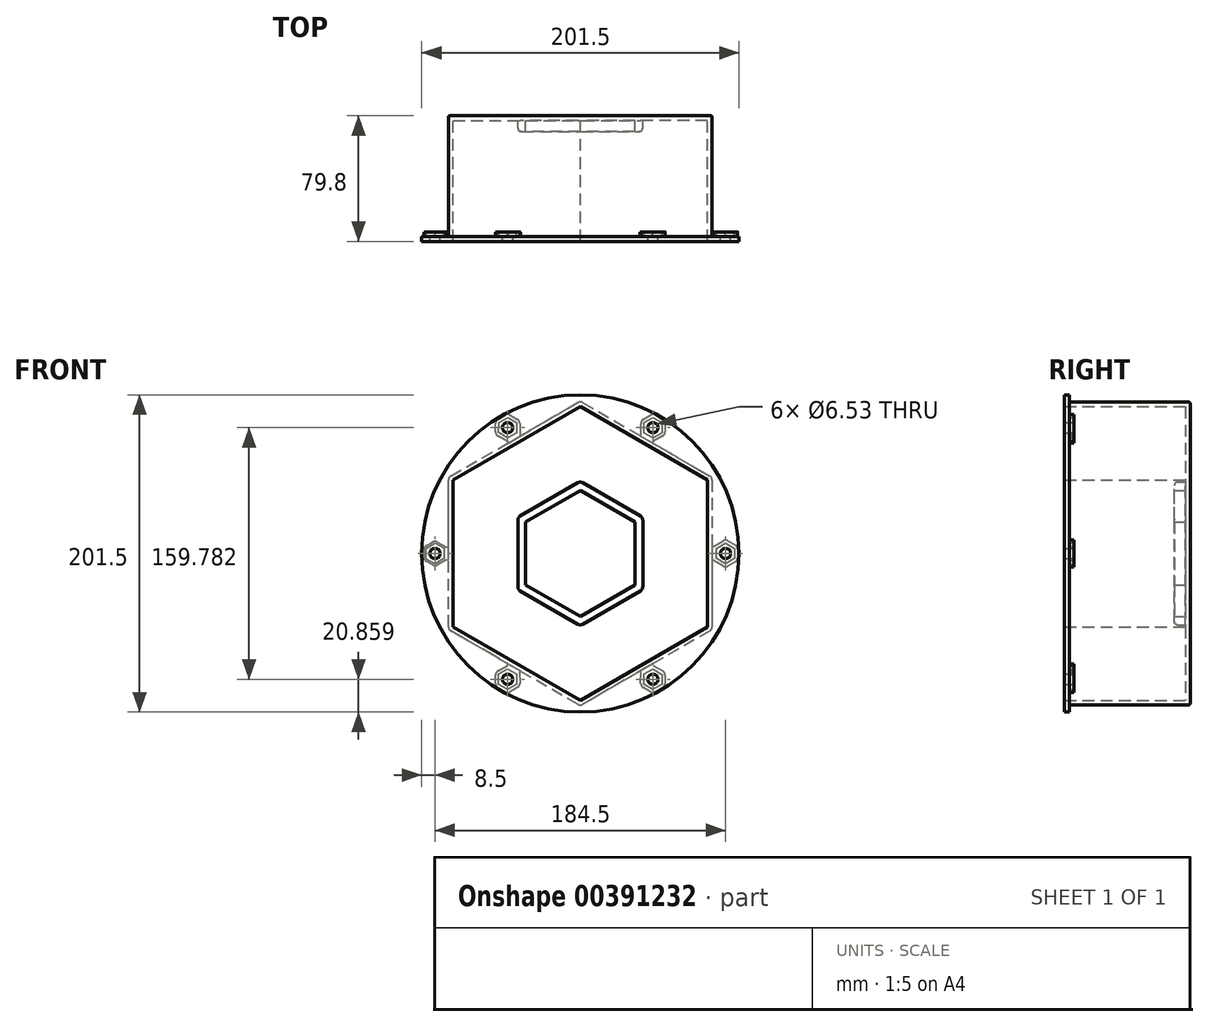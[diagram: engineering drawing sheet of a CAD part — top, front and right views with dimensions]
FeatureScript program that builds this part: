
annotation { "Feature Type Name" : "Feature", "Feature Type Description" : "" }
export const myFeature = defineFeature(function(context is Context, id is Id, definition is map)
    precondition{}
    {
        {
            var Q0;
            Q0=qCreatedBy(makeId("Front.planeOp"),FACE);
            var sketch = newSketch(context, id + "F0", { "sketchPlane" : qUnion([Q0])});
            skCircle(sketch, "E0.cCircle", {"center": v(0, 0) * mm, "radius": 80.75 * mm, "construction": true});
            skLineSegment(sketch, "E0.0", {"start": v(80.75, -46.62) * mm, "end": v(0, -93.24) * mm});
            skLineSegment(sketch, "E0.1", {"start": v(0, -93.24) * mm, "end": v(-80.75, -46.62) * mm});
            skLineSegment(sketch, "E0.2", {"start": v(-80.75, -46.62) * mm, "end": v(-80.75, 46.62) * mm});
            skLineSegment(sketch, "E0.3", {"start": v(-80.75, 46.62) * mm, "end": v(0, 93.24) * mm});
            skLineSegment(sketch, "E0.4", {"start": v(0, 93.24) * mm, "end": v(80.75, 46.62) * mm});
            skLineSegment(sketch, "E0.5", {"start": v(80.75, 46.62) * mm, "end": v(80.75, -46.62) * mm});
            skPoint(sketch, "E0.0.midPoint", {"position": v(40.38, -69.93) * mm});
            skCircle(sketch, "E1.cCircle", {"center": v(0, 0) * mm, "radius": 83.75 * mm, "construction": true});
            skLineSegment(sketch, "E1.0", {"start": v(83.75, 46.62) * mm, "end": v(83.75, -46.62) * mm});
            skLineSegment(sketch, "E1.1", {"start": v(82.25, -49.22) * mm, "end": v(1.5, -95.84) * mm});
            skLineSegment(sketch, "E1.2", {"start": v(-1.5, -95.84) * mm, "end": v(-82.25, -49.22) * mm});
            skLineSegment(sketch, "E1.3", {"start": v(-83.75, -46.62) * mm, "end": v(-83.75, 46.62) * mm});
            skLineSegment(sketch, "E1.4", {"start": v(-82.25, 49.22) * mm, "end": v(-1.5, 95.84) * mm});
            skLineSegment(sketch, "E1.5", {"start": v(1.5, 95.84) * mm, "end": v(82.25, 49.22) * mm});
            skPoint(sketch, "E1.0.midPoint", {"position": v(83.75, 0) * mm});
            skCircle(sketch, "E2", {"center": v(0, 0) * mm, "radius": 100.75 * mm});
            skCircle(sketch, "E3.cCircle", {"center": v(0, 0) * mm, "radius": 39.66 * mm, "construction": true});
            skLineSegment(sketch, "E3.0", {"start": v(38.16, -23.77) * mm, "end": v(1.5, -44.93) * mm});
            skLineSegment(sketch, "E3.1", {"start": v(-1.5, -44.93) * mm, "end": v(-38.16, -23.77) * mm});
            skLineSegment(sketch, "E3.2", {"start": v(-39.66, -21.17) * mm, "end": v(-39.66, 21.17) * mm});
            skLineSegment(sketch, "E3.3", {"start": v(-38.16, 23.77) * mm, "end": v(-1.5, 44.93) * mm});
            skLineSegment(sketch, "E3.4", {"start": v(1.5, 44.93) * mm, "end": v(38.16, 23.77) * mm});
            skLineSegment(sketch, "E3.5", {"start": v(39.66, 21.17) * mm, "end": v(39.66, -21.17) * mm});
            skPoint(sketch, "E3.0.midPoint", {"position": v(19.83, -34.35) * mm});
            skCircle(sketch, "E4.cCircle", {"center": v(0, 0) * mm, "radius": 34.66 * mm, "construction": true});
            skLineSegment(sketch, "E4.0", {"start": v(34.66, -20.01) * mm, "end": v(0, -40.03) * mm});
            skLineSegment(sketch, "E4.1", {"start": v(0, -40.03) * mm, "end": v(-34.66, -20.01) * mm});
            skLineSegment(sketch, "E4.2", {"start": v(-34.66, -20.01) * mm, "end": v(-34.66, 20.01) * mm});
            skLineSegment(sketch, "E4.3", {"start": v(-34.66, 20.01) * mm, "end": v(0, 40.03) * mm});
            skLineSegment(sketch, "E4.4", {"start": v(0, 40.03) * mm, "end": v(34.66, 20.01) * mm});
            skLineSegment(sketch, "E4.5", {"start": v(34.66, 20.01) * mm, "end": v(34.66, -20.01) * mm});
            skPoint(sketch, "E4.0.midPoint", {"position": v(17.33, -30.02) * mm});
            skPoint(sketch, "E5.visualSharp", {"position": v(0, 96.7) * mm});
            skArc(sketch, "E5.filletArc", {"start": v(1.5, 95.84) * mm, "mid": v(0, 96.24) * mm, "end": v(-1.5, 95.84) * mm});
            skPoint(sketch, "E6.visualSharp", {"position": v(83.75, 48.35) * mm});
            skArc(sketch, "E6.filletArc", {"start": v(83.75, 46.62) * mm, "mid": v(83.35, 48.12) * mm, "end": v(82.25, 49.22) * mm});
            skPoint(sketch, "E7.visualSharp", {"position": v(83.75, -48.35) * mm});
            skArc(sketch, "E7.filletArc", {"start": v(82.25, -49.22) * mm, "mid": v(83.35, -48.12) * mm, "end": v(83.75, -46.62) * mm});
            skPoint(sketch, "E8.visualSharp", {"position": v(0, -96.7) * mm});
            skArc(sketch, "E8.filletArc", {"start": v(-1.5, -95.84) * mm, "mid": v(0, -96.24) * mm, "end": v(1.5, -95.84) * mm});
            skPoint(sketch, "E9.visualSharp", {"position": v(-83.75, -48.35) * mm});
            skArc(sketch, "E9.filletArc", {"start": v(-83.75, -46.62) * mm, "mid": v(-83.35, -48.12) * mm, "end": v(-82.25, -49.22) * mm});
            skPoint(sketch, "E10.visualSharp", {"position": v(-83.75, 48.35) * mm});
            skArc(sketch, "E10.filletArc", {"start": v(-82.25, 49.22) * mm, "mid": v(-83.35, 48.12) * mm, "end": v(-83.75, 46.62) * mm});
            skPoint(sketch, "E11.visualSharp", {"position": v(39.66, 22.9) * mm});
            skArc(sketch, "E11.filletArc", {"start": v(39.66, 21.17) * mm, "mid": v(39.26, 22.67) * mm, "end": v(38.16, 23.77) * mm});
            skPoint(sketch, "E12.visualSharp", {"position": v(39.66, -22.9) * mm});
            skArc(sketch, "E12.filletArc", {"start": v(38.16, -23.77) * mm, "mid": v(39.26, -22.67) * mm, "end": v(39.66, -21.17) * mm});
            skPoint(sketch, "E13.visualSharp", {"position": v(0, -45.8) * mm});
            skArc(sketch, "E13.filletArc", {"start": v(-1.5, -44.93) * mm, "mid": v(0, -45.34) * mm, "end": v(1.5, -44.93) * mm});
            skPoint(sketch, "E14.visualSharp", {"position": v(-39.66, -22.9) * mm});
            skArc(sketch, "E14.filletArc", {"start": v(-39.66, -21.17) * mm, "mid": v(-39.26, -22.67) * mm, "end": v(-38.16, -23.77) * mm});
            skPoint(sketch, "E15.visualSharp", {"position": v(-39.66, 22.9) * mm});
            skArc(sketch, "E15.filletArc", {"start": v(-38.16, 23.77) * mm, "mid": v(-39.26, 22.67) * mm, "end": v(-39.66, 21.17) * mm});
            skPoint(sketch, "E16.visualSharp", {"position": v(0, 45.8) * mm});
            skArc(sketch, "E16.filletArc", {"start": v(1.5, 44.93) * mm, "mid": v(0, 45.34) * mm, "end": v(-1.5, 44.93) * mm});
            skPoint(sketch, "E17", {"position": v(-46.13, 79.9) * mm});
            skPoint(sketch, "E18", {"position": v(-92.25, 0) * mm});
            skPoint(sketch, "E19", {"position": v(-46.12, -79.9) * mm});
            skPoint(sketch, "E20", {"position": v(46.13, -79.9) * mm});
            skPoint(sketch, "E21", {"position": v(92.25, 0) * mm});
            skPoint(sketch, "E22", {"position": v(46.13, 79.9) * mm});
            skCircle(sketch, "E23.cCircle", {"center": v(92.25, 0) * mm, "radius": 5.7 * mm, "construction": true});
            skLineSegment(sketch, "E23.0", {"start": v(97.95, -3.3) * mm, "end": v(92.25, -6.58) * mm});
            skLineSegment(sketch, "E23.1", {"start": v(92.25, -6.58) * mm, "end": v(86.55, -3.3) * mm});
            skLineSegment(sketch, "E23.2", {"start": v(86.55, -3.3) * mm, "end": v(86.55, 3.3) * mm});
            skLineSegment(sketch, "E23.3", {"start": v(86.55, 3.3) * mm, "end": v(92.25, 6.58) * mm});
            skLineSegment(sketch, "E23.4", {"start": v(92.25, 6.58) * mm, "end": v(97.95, 3.3) * mm});
            skLineSegment(sketch, "E23.5", {"start": v(97.95, 3.3) * mm, "end": v(97.95, -3.3) * mm});
            skPoint(sketch, "E23.0.midPoint", {"position": v(95.1, -4.94) * mm});
            skCircle(sketch, "E24.cCircle", {"center": v(46.13, 79.9) * mm, "radius": 5.7 * mm, "construction": true});
            skLineSegment(sketch, "E24.0", {"start": v(51.83, 83.18) * mm, "end": v(51.83, 76.6) * mm});
            skLineSegment(sketch, "E24.1", {"start": v(51.83, 76.6) * mm, "end": v(46.13, 73.3) * mm});
            skLineSegment(sketch, "E24.2", {"start": v(46.13, 73.3) * mm, "end": v(40.43, 76.6) * mm});
            skLineSegment(sketch, "E24.3", {"start": v(40.43, 76.6) * mm, "end": v(40.43, 83.18) * mm});
            skLineSegment(sketch, "E24.4", {"start": v(40.43, 83.18) * mm, "end": v(46.12, 86.47) * mm});
            skLineSegment(sketch, "E24.5", {"start": v(46.13, 86.47) * mm, "end": v(51.83, 83.18) * mm});
            skPoint(sketch, "E24.0.midPoint", {"position": v(51.83, 79.9) * mm});
            skCircle(sketch, "E25.cCircle", {"center": v(-46.13, 79.9) * mm, "radius": 5.7 * mm, "construction": true});
            skLineSegment(sketch, "E25.0", {"start": v(-40.5, 76.48) * mm, "end": v(-46.26, 73.31) * mm});
            skLineSegment(sketch, "E25.1", {"start": v(-46.26, 73.31) * mm, "end": v(-51.9, 76.72) * mm});
            skLineSegment(sketch, "E25.2", {"start": v(-51.9, 76.72) * mm, "end": v(-51.76, 83.3) * mm});
            skLineSegment(sketch, "E25.3", {"start": v(-51.76, 83.3) * mm, "end": v(-45.99, 86.47) * mm});
            skLineSegment(sketch, "E25.4", {"start": v(-45.99, 86.47) * mm, "end": v(-40.36, 83.06) * mm});
            skLineSegment(sketch, "E25.5", {"start": v(-40.36, 83.06) * mm, "end": v(-40.5, 76.48) * mm});
            skPoint(sketch, "E25.0.midPoint", {"position": v(-43.38, 74.9) * mm});
            skCircle(sketch, "E26.cCircle", {"center": v(-92.25, 0) * mm, "radius": 5.7 * mm, "construction": true});
            skLineSegment(sketch, "E26.0", {"start": v(-86.5, -3.22) * mm, "end": v(-92.16, -6.58) * mm});
            skLineSegment(sketch, "E26.1", {"start": v(-92.16, -6.58) * mm, "end": v(-97.9, -3.37) * mm});
            skLineSegment(sketch, "E26.2", {"start": v(-97.9, -3.37) * mm, "end": v(-98, 3.22) * mm});
            skLineSegment(sketch, "E26.3", {"start": v(-98, 3.22) * mm, "end": v(-92.34, 6.58) * mm});
            skLineSegment(sketch, "E26.4", {"start": v(-92.34, 6.58) * mm, "end": v(-86.6, 3.37) * mm});
            skLineSegment(sketch, "E26.5", {"start": v(-86.6, 3.37) * mm, "end": v(-86.5, -3.22) * mm});
            skPoint(sketch, "E26.0.midPoint", {"position": v(-89.34, -4.9) * mm});
            skCircle(sketch, "E27.cCircle", {"center": v(46.13, -79.9) * mm, "radius": 5.7 * mm, "construction": true});
            skLineSegment(sketch, "E27.0", {"start": v(51.77, -83.28) * mm, "end": v(46, -86.47) * mm});
            skLineSegment(sketch, "E27.1", {"start": v(46, -86.47) * mm, "end": v(40.37, -83.08) * mm});
            skLineSegment(sketch, "E27.2", {"start": v(40.37, -83.08) * mm, "end": v(40.48, -76.5) * mm});
            skLineSegment(sketch, "E27.3", {"start": v(40.48, -76.5) * mm, "end": v(46.24, -73.31) * mm});
            skLineSegment(sketch, "E27.4", {"start": v(46.24, -73.31) * mm, "end": v(51.88, -76.7) * mm});
            skLineSegment(sketch, "E27.5", {"start": v(51.88, -76.7) * mm, "end": v(51.77, -83.28) * mm});
            skPoint(sketch, "E27.0.midPoint", {"position": v(48.89, -84.88) * mm});
            skCircle(sketch, "E28.cCircle", {"center": v(-46.12, -79.9) * mm, "radius": 5.7 * mm, "construction": true});
            skLineSegment(sketch, "E28.0", {"start": v(-40.4, -83.14) * mm, "end": v(-46.07, -86.47) * mm});
            skLineSegment(sketch, "E28.1", {"start": v(-46.07, -86.47) * mm, "end": v(-51.8, -83.23) * mm});
            skLineSegment(sketch, "E28.2", {"start": v(-51.8, -83.23) * mm, "end": v(-51.85, -76.65) * mm});
            skLineSegment(sketch, "E28.3", {"start": v(-51.85, -76.65) * mm, "end": v(-46.18, -73.3) * mm});
            skLineSegment(sketch, "E28.4", {"start": v(-46.18, -73.3) * mm, "end": v(-40.45, -76.55) * mm});
            skLineSegment(sketch, "E28.5", {"start": v(-40.45, -76.55) * mm, "end": v(-40.4, -83.14) * mm});
            skPoint(sketch, "E28.0.midPoint", {"position": v(-43.24, -84.8) * mm});
            skCircle(sketch, "E29.cCircle", {"center": v(46.13, -79.9) * mm, "radius": 7.7 * mm, "construction": true});
            skLineSegment(sketch, "E29.0", {"start": v(53.87, -77.31) * mm, "end": v(53.78, -82.74) * mm});
            skLineSegment(sketch, "E29.1", {"start": v(52.23, -85.31) * mm, "end": v(47.48, -87.94) * mm});
            skLineSegment(sketch, "E29.2", {"start": v(44.48, -87.89) * mm, "end": v(39.83, -85.1) * mm});
            skLineSegment(sketch, "E29.3", {"start": v(38.38, -82.47) * mm, "end": v(38.5, -75.3) * mm});
            skLineSegment(sketch, "E29.4", {"start": v(38.5, -75.3) * mm, "end": v(46.28, -71) * mm});
            skLineSegment(sketch, "E29.5", {"start": v(46.28, -71) * mm, "end": v(52.42, -74.7) * mm});
            skPoint(sketch, "E29.0.midPoint", {"position": v(53.82, -80.03) * mm});
            skCircle(sketch, "E30.cCircle", {"center": v(-46.12, -79.9) * mm, "radius": 7.7 * mm, "construction": true});
            skLineSegment(sketch, "E30.0", {"start": v(-39.88, -85.15) * mm, "end": v(-44.56, -87.9) * mm});
            skLineSegment(sketch, "E30.1", {"start": v(-47.56, -87.93) * mm, "end": v(-52.28, -85.25) * mm});
            skLineSegment(sketch, "E30.2", {"start": v(-53.8, -82.67) * mm, "end": v(-53.85, -77.24) * mm});
            skLineSegment(sketch, "E30.3", {"start": v(-52.37, -74.63) * mm, "end": v(-46.2, -71) * mm});
            skLineSegment(sketch, "E30.4", {"start": v(-46.2, -71) * mm, "end": v(-38.46, -75.38) * mm});
            skLineSegment(sketch, "E30.5", {"start": v(-38.46, -75.38) * mm, "end": v(-38.4, -82.54) * mm});
            skPoint(sketch, "E30.0.midPoint", {"position": v(-42.22, -86.53) * mm});
            skCircle(sketch, "E31.cCircle", {"center": v(-92.25, 0) * mm, "radius": 7.05 * mm, "construction": true});
            skLineSegment(sketch, "E31.0", {"start": v(-85.15, -3.98) * mm, "end": v(-90.66, -7.25) * mm});
            skLineSegment(sketch, "E31.1", {"start": v(-93.65, -7.3) * mm, "end": v(-97.73, -5) * mm});
            skLineSegment(sketch, "E31.2", {"start": v(-99.27, -2.43) * mm, "end": v(-99.33, 2.24) * mm});
            skLineSegment(sketch, "E31.3", {"start": v(-97.86, 4.86) * mm, "end": v(-93.84, 7.25) * mm});
            skLineSegment(sketch, "E31.4", {"start": v(-90.85, 7.3) * mm, "end": v(-85.26, 4.16) * mm});
            skLineSegment(sketch, "E31.5", {"start": v(-85.26, 4.16) * mm, "end": v(-85.15, -3.98) * mm});
            skPoint(sketch, "E31.0.midPoint", {"position": v(-88.65, -6.06) * mm});
            skCircle(sketch, "E32.cCircle", {"center": v(-46.13, 79.9) * mm, "radius": 7.7 * mm, "construction": true});
            skLineSegment(sketch, "E32.0", {"start": v(-53.83, 77.18) * mm, "end": v(-53.83, 82.6) * mm});
            skLineSegment(sketch, "E32.1", {"start": v(-52.33, 85.2) * mm, "end": v(-47.63, 87.92) * mm});
            skLineSegment(sketch, "E32.2", {"start": v(-44.63, 87.92) * mm, "end": v(-39.93, 85.2) * mm});
            skLineSegment(sketch, "E32.3", {"start": v(-38.43, 82.6) * mm, "end": v(-38.43, 75.45) * mm});
            skLineSegment(sketch, "E32.4", {"start": v(-38.43, 75.45) * mm, "end": v(-46.13, 71) * mm});
            skLineSegment(sketch, "E32.5", {"start": v(-46.13, 71) * mm, "end": v(-52.33, 74.58) * mm});
            skPoint(sketch, "E32.0.midPoint", {"position": v(-53.83, 79.9) * mm});
            skCircle(sketch, "E33.cCircle", {"center": v(46.13, 79.9) * mm, "radius": 7.7 * mm, "construction": true});
            skLineSegment(sketch, "E33.0", {"start": v(52.33, 74.58) * mm, "end": v(46.13, 71) * mm});
            skLineSegment(sketch, "E33.1", {"start": v(46.13, 71) * mm, "end": v(38.43, 75.45) * mm});
            skLineSegment(sketch, "E33.2", {"start": v(38.43, 75.45) * mm, "end": v(38.43, 82.6) * mm});
            skLineSegment(sketch, "E33.3", {"start": v(39.93, 85.2) * mm, "end": v(44.62, 87.92) * mm});
            skLineSegment(sketch, "E33.4", {"start": v(47.62, 87.92) * mm, "end": v(52.33, 85.2) * mm});
            skLineSegment(sketch, "E33.5", {"start": v(53.83, 82.6) * mm, "end": v(53.83, 77.18) * mm});
            skPoint(sketch, "E33.0.midPoint", {"position": v(49.98, 73.22) * mm});
            skCircle(sketch, "E34.cCircle", {"center": v(92.25, 0) * mm, "radius": 7.7 * mm, "construction": true});
            skLineSegment(sketch, "E34.0", {"start": v(99.95, 2.71) * mm, "end": v(99.95, -2.71) * mm});
            skLineSegment(sketch, "E34.1", {"start": v(98.45, -5.31) * mm, "end": v(93.75, -8.03) * mm});
            skLineSegment(sketch, "E34.2", {"start": v(90.75, -8.03) * mm, "end": v(84.55, -4.45) * mm});
            skLineSegment(sketch, "E34.3", {"start": v(84.55, -4.45) * mm, "end": v(84.55, 4.45) * mm});
            skLineSegment(sketch, "E34.4", {"start": v(84.55, 4.45) * mm, "end": v(90.75, 8.03) * mm});
            skLineSegment(sketch, "E34.5", {"start": v(93.75, 8.03) * mm, "end": v(98.45, 5.31) * mm});
            skPoint(sketch, "E34.0.midPoint", {"position": v(99.95, 0) * mm});
            skLineSegment(sketch, "E35", {"start": v(84.55, -4.45) * mm, "end": v(83.75, -4.45) * mm});
            skLineSegment(sketch, "E36", {"start": v(84.55, 4.45) * mm, "end": v(83.75, 4.45) * mm});
            skPoint(sketch, "E37.visualSharp", {"position": v(92.25, 8.9) * mm});
            skArc(sketch, "E37.filletArc", {"start": v(93.75, 8.03) * mm, "mid": v(92.25, 8.43) * mm, "end": v(90.75, 8.03) * mm});
            skPoint(sketch, "E38.visualSharp", {"position": v(99.95, 4.45) * mm});
            skArc(sketch, "E38.filletArc", {"start": v(99.95, 2.71) * mm, "mid": v(99.55, 4.21) * mm, "end": v(98.45, 5.31) * mm});
            skPoint(sketch, "E39.visualSharp", {"position": v(99.95, -4.45) * mm});
            skArc(sketch, "E39.filletArc", {"start": v(98.45, -5.31) * mm, "mid": v(99.55, -4.21) * mm, "end": v(99.95, -2.71) * mm});
            skPoint(sketch, "E40.visualSharp", {"position": v(92.25, -8.9) * mm});
            skArc(sketch, "E40.filletArc", {"start": v(90.75, -8.03) * mm, "mid": v(92.25, -8.43) * mm, "end": v(93.75, -8.03) * mm});
            skPoint(sketch, "E41.visualSharp", {"position": v(38.43, 84.34) * mm});
            skArc(sketch, "E41.filletArc", {"start": v(39.93, 85.2) * mm, "mid": v(38.83, 84.1) * mm, "end": v(38.43, 82.6) * mm});
            skPoint(sketch, "E42.visualSharp", {"position": v(46.12, 88.78) * mm});
            skArc(sketch, "E42.filletArc", {"start": v(47.62, 87.92) * mm, "mid": v(46.12, 88.32) * mm, "end": v(44.62, 87.92) * mm});
            skPoint(sketch, "E43.visualSharp", {"position": v(53.83, 84.34) * mm});
            skArc(sketch, "E43.filletArc", {"start": v(53.83, 82.6) * mm, "mid": v(53.42, 84.1) * mm, "end": v(52.33, 85.2) * mm});
            skPoint(sketch, "E44.visualSharp", {"position": v(53.83, 75.45) * mm});
            skArc(sketch, "E44.filletArc", {"start": v(52.33, 74.58) * mm, "mid": v(53.42, 75.68) * mm, "end": v(53.83, 77.18) * mm});
            skLineSegment(sketch, "E45", {"start": v(38.43, 75.45) * mm, "end": v(38.03, 74.75) * mm});
            skLineSegment(sketch, "E46", {"start": v(46.13, 71) * mm, "end": v(45.73, 70.3) * mm});
            skPoint(sketch, "E47.visualSharp", {"position": v(-46.13, 88.78) * mm});
            skArc(sketch, "E47.filletArc", {"start": v(-44.63, 87.92) * mm, "mid": v(-46.13, 88.32) * mm, "end": v(-47.63, 87.92) * mm});
            skPoint(sketch, "E48.visualSharp", {"position": v(-38.43, 84.34) * mm});
            skArc(sketch, "E48.filletArc", {"start": v(-38.43, 82.6) * mm, "mid": v(-38.83, 84.1) * mm, "end": v(-39.93, 85.2) * mm});
            skPoint(sketch, "E49.visualSharp", {"position": v(-53.83, 84.34) * mm});
            skArc(sketch, "E49.filletArc", {"start": v(-52.33, 85.2) * mm, "mid": v(-53.42, 84.1) * mm, "end": v(-53.83, 82.6) * mm});
            skPoint(sketch, "E50.visualSharp", {"position": v(-53.83, 75.45) * mm});
            skArc(sketch, "E50.filletArc", {"start": v(-53.83, 77.18) * mm, "mid": v(-53.42, 75.68) * mm, "end": v(-52.33, 74.58) * mm});
            skLineSegment(sketch, "E51", {"start": v(-46.13, 71) * mm, "end": v(-45.73, 70.3) * mm});
            skLineSegment(sketch, "E52", {"start": v(-38.43, 75.45) * mm, "end": v(-38.03, 74.75) * mm});
            skPoint(sketch, "E53.visualSharp", {"position": v(-92.36, 8.14) * mm});
            skArc(sketch, "E53.filletArc", {"start": v(-90.85, 7.3) * mm, "mid": v(-92.35, 7.67) * mm, "end": v(-93.84, 7.25) * mm});
            skPoint(sketch, "E54.visualSharp", {"position": v(-99.35, 3.98) * mm});
            skArc(sketch, "E54.filletArc", {"start": v(-97.86, 4.86) * mm, "mid": v(-98.94, 3.75) * mm, "end": v(-99.33, 2.24) * mm});
            skPoint(sketch, "E55.visualSharp", {"position": v(-99.24, -4.16) * mm});
            skArc(sketch, "E55.filletArc", {"start": v(-99.27, -2.43) * mm, "mid": v(-98.84, -3.92) * mm, "end": v(-97.73, -5) * mm});
            skPoint(sketch, "E56.visualSharp", {"position": v(-92.14, -8.14) * mm});
            skArc(sketch, "E56.filletArc", {"start": v(-93.65, -7.3) * mm, "mid": v(-92.15, -7.67) * mm, "end": v(-90.66, -7.25) * mm});
            skLineSegment(sketch, "E57", {"start": v(-85.26, 4.16) * mm, "end": v(-83.75, 4.18) * mm});
            skLineSegment(sketch, "E58", {"start": v(-85.15, -3.98) * mm, "end": v(-83.75, -3.96) * mm});
            skPoint(sketch, "E59.visualSharp", {"position": v(-53.86, -75.5) * mm});
            skArc(sketch, "E59.filletArc", {"start": v(-52.37, -74.63) * mm, "mid": v(-53.46, -75.74) * mm, "end": v(-53.85, -77.24) * mm});
            skPoint(sketch, "E60.visualSharp", {"position": v(-53.79, -84.4) * mm});
            skArc(sketch, "E60.filletArc", {"start": v(-53.8, -82.67) * mm, "mid": v(-53.39, -84.16) * mm, "end": v(-52.28, -85.25) * mm});
            skPoint(sketch, "E61.visualSharp", {"position": v(-46.05, -88.78) * mm});
            skArc(sketch, "E61.filletArc", {"start": v(-47.56, -87.93) * mm, "mid": v(-46.06, -88.32) * mm, "end": v(-44.56, -87.9) * mm});
            skPoint(sketch, "E62.visualSharp", {"position": v(-38.4, -84.28) * mm});
            skArc(sketch, "E62.filletArc", {"start": v(-39.88, -85.15) * mm, "mid": v(-38.8, -84.05) * mm, "end": v(-38.4, -82.54) * mm});
            skLineSegment(sketch, "E63", {"start": v(-46.2, -71) * mm, "end": v(-45.78, -70.27) * mm});
            skLineSegment(sketch, "E64", {"start": v(-38.46, -75.38) * mm, "end": v(-38.08, -74.72) * mm});
            skPoint(sketch, "E65.visualSharp", {"position": v(53.9, -75.58) * mm});
            skArc(sketch, "E65.filletArc", {"start": v(53.87, -77.31) * mm, "mid": v(53.5, -75.8) * mm, "end": v(52.42, -74.7) * mm});
            skPoint(sketch, "E66.visualSharp", {"position": v(53.74, -84.47) * mm});
            skArc(sketch, "E66.filletArc", {"start": v(52.23, -85.31) * mm, "mid": v(53.35, -84.23) * mm, "end": v(53.78, -82.74) * mm});
            skPoint(sketch, "E67.visualSharp", {"position": v(45.97, -88.78) * mm});
            skArc(sketch, "E67.filletArc", {"start": v(44.48, -87.89) * mm, "mid": v(45.97, -88.32) * mm, "end": v(47.48, -87.94) * mm});
            skPoint(sketch, "E68.visualSharp", {"position": v(38.35, -84.2) * mm});
            skArc(sketch, "E68.filletArc", {"start": v(38.38, -82.47) * mm, "mid": v(38.75, -83.97) * mm, "end": v(39.83, -85.1) * mm});
            skLineSegment(sketch, "E69", {"start": v(38.5, -75.3) * mm, "end": v(38.14, -74.68) * mm});
            skLineSegment(sketch, "E70", {"start": v(46.28, -71) * mm, "end": v(45.86, -70.23) * mm});
            skSolve(sketch);
        }
        {
            var Q0;
            Q0=makeQuery(id+"F0.imprint","IMPRINT",FACE,{"disambiguationData":[TD([[makeQuery(id+"F0.imprint","IMPRINT",EDGE,{"derivedFrom":sQuery(id+"F0.wireOp",EDGE,"E0.0")}),-1.0]])]});
            var Q1;
            Q1=makeQuery(id+"F0.imprint","IMPRINT",FACE,{"disambiguationData":[TD([[makeQuery(id+"F0.imprint","IMPRINT",EDGE,{"derivedFrom":sQuery(id+"F0.wireOp",EDGE,"E4.0")}),-1.0]])]});
            extrude(context, id + "F1", {"entities" : qUnion([Q0, Q1]), "depth" : 3 * mm});
        }
        {
            var Q0;
            Q0=makeQuery(id+"F0.imprint","IMPRINT",FACE,{"disambiguationData":[TD([[makeQuery(id+"F0.imprint","IMPRINT",EDGE,{"derivedFrom":sQuery(id+"F0.wireOp",EDGE,"E3.0")}),-1.0]])]});
            extrude(context, id + "F2", {"entities" : qUnion([Q0]), "depth" : 10 * mm});
        }
        {
            var Q0;
            Q0=makeQuery(id+"F0.imprint","IMPRINT",FACE,{"disambiguationData":[TD([[makeQuery(id+"F0.imprint","IMPRINT",EDGE,{"derivedFrom":sQuery(id+"F0.wireOp",EDGE,"E0.0")}),1.0]])]});
            extrude(context, id + "F3", {"entities" : qUnion([Q0]), "operationType" : NewBodyOperationType.ADD, "depth" : 79.8 * mm});
        }
        {
            var Q0;
            Q0=makeQuery(id+"F0.imprint","IMPRINT",FACE,{"disambiguationData":[TD([[makeQuery(id+"F0.imprint","IMPRINT",EDGE,{"derivedFrom":sQuery(id+"F0.wireOp",EDGE,"E1.0")}),1.0]])]});
            var Q1;
            Q1=makeQuery(id+"F0.imprint","IMPRINT",FACE,{"disambiguationData":[TD([[makeQuery(id+"F0.imprint","IMPRINT",EDGE,{"derivedFrom":sQuery(id+"F0.wireOp",EDGE,"E25.0")}),-1.0]])]});
            var Q2;
            Q2=makeQuery(id+"F0.imprint","IMPRINT",FACE,{"disambiguationData":[TD([[makeQuery(id+"F0.imprint","IMPRINT",EDGE,{"derivedFrom":sQuery(id+"F0.wireOp",EDGE,"E24.0")}),-1.0]])]});
            var Q3;
            Q3=makeQuery(id+"F0.imprint","IMPRINT",FACE,{"disambiguationData":[TD([[makeQuery(id+"F0.imprint","IMPRINT",EDGE,{"derivedFrom":sQuery(id+"F0.wireOp",EDGE,"E23.0")}),-1.0]])]});
            var Q4;
            Q4=makeQuery(id+"F0.imprint","IMPRINT",FACE,{"disambiguationData":[TD([[makeQuery(id+"F0.imprint","IMPRINT",EDGE,{"derivedFrom":sQuery(id+"F0.wireOp",EDGE,"E27.0")}),-1.0]])]});
            var Q5;
            Q5=makeQuery(id+"F0.imprint","IMPRINT",FACE,{"disambiguationData":[TD([[makeQuery(id+"F0.imprint","IMPRINT",EDGE,{"derivedFrom":sQuery(id+"F0.wireOp",EDGE,"E28.0")}),-1.0]])]});
            var Q6;
            Q6=makeQuery(id+"F0.imprint","IMPRINT",FACE,{"disambiguationData":[TD([[makeQuery(id+"F0.imprint","IMPRINT",EDGE,{"derivedFrom":sQuery(id+"F0.wireOp",EDGE,"E26.0")}),-1.0]])]});
            extrude(context, id + "F4", {"entities" : qUnion([Q0, Q1, Q2, Q3, Q4, Q5, Q6]), "operationType" : NewBodyOperationType.ADD, "depth" : 79.8 * mm, "hasSecondDirection" : true, "secondDirectionOppositeDirection" : false, "secondDirectionDepth" : 76.8 * mm});
        }
        {
            var Q0;
            Q0=makeQuery(id+"F2.opExtrude","CAP_EDGE",EDGE,{"disambiguationData":[OSD([sQuery(id+"F0.wireOp",EDGE,"E3.4")])],"isStart":false});
            fillet(context, id + "F5", {"entities" : qUnion([Q0]), "radius" : 2 * mm, "tangentPropagation" : true, "allowEdgeOverflow" : false});
        }
        {
            var Q0;
            Q0=makeQuery(id+"F0.imprint","IMPRINT",FACE,{"disambiguationData":[TD([[makeQuery(id+"F0.imprint","IMPRINT",EDGE,{"derivedFrom":sQuery(id+"F0.wireOp",EDGE,"E25.0")}),1.0]])]});
            var Q1;
            Q1=makeQuery(id+"F0.imprint","IMPRINT",FACE,{"disambiguationData":[TD([[makeQuery(id+"F0.imprint","IMPRINT",EDGE,{"derivedFrom":sQuery(id+"F0.wireOp",EDGE,"E32.4")}),1.0]])]});
            var Q2;
            Q2=makeQuery(id+"F0.imprint","IMPRINT",FACE,{"disambiguationData":[TD([[makeQuery(id+"F0.imprint","IMPRINT",EDGE,{"derivedFrom":sQuery(id+"F0.wireOp",EDGE,"E24.0")}),1.0]])]});
            var Q3;
            Q3=makeQuery(id+"F0.imprint","IMPRINT",FACE,{"disambiguationData":[TD([[makeQuery(id+"F0.imprint","IMPRINT",EDGE,{"derivedFrom":sQuery(id+"F0.wireOp",EDGE,"E33.1")}),1.0]])]});
            var Q4;
            Q4=makeQuery(id+"F0.imprint","IMPRINT",FACE,{"disambiguationData":[TD([[makeQuery(id+"F0.imprint","IMPRINT",EDGE,{"derivedFrom":sQuery(id+"F0.wireOp",EDGE,"E23.0")}),1.0]])]});
            var Q5;
            Q5=makeQuery(id+"F0.imprint","IMPRINT",FACE,{"disambiguationData":[TD([[makeQuery(id+"F0.imprint","IMPRINT",EDGE,{"derivedFrom":sQuery(id+"F0.wireOp",EDGE,"E34.3")}),1.0]])]});
            var Q6;
            Q6=makeQuery(id+"F0.imprint","IMPRINT",FACE,{"disambiguationData":[TD([[makeQuery(id+"F0.imprint","IMPRINT",EDGE,{"derivedFrom":sQuery(id+"F0.wireOp",EDGE,"E27.0")}),1.0]])]});
            var Q7;
            Q7=makeQuery(id+"F0.imprint","IMPRINT",FACE,{"disambiguationData":[TD([[makeQuery(id+"F0.imprint","IMPRINT",EDGE,{"derivedFrom":sQuery(id+"F0.wireOp",EDGE,"E29.4")}),1.0]])]});
            var Q8;
            Q8=makeQuery(id+"F0.imprint","IMPRINT",FACE,{"disambiguationData":[TD([[makeQuery(id+"F0.imprint","IMPRINT",EDGE,{"derivedFrom":sQuery(id+"F0.wireOp",EDGE,"E28.0")}),1.0]])]});
            var Q9;
            Q9=makeQuery(id+"F0.imprint","IMPRINT",FACE,{"disambiguationData":[TD([[makeQuery(id+"F0.imprint","IMPRINT",EDGE,{"derivedFrom":sQuery(id+"F0.wireOp",EDGE,"E30.4")}),1.0]])]});
            var Q10;
            Q10=makeQuery(id+"F0.imprint","IMPRINT",FACE,{"disambiguationData":[TD([[makeQuery(id+"F0.imprint","IMPRINT",EDGE,{"derivedFrom":sQuery(id+"F0.wireOp",EDGE,"E26.0")}),1.0]])]});
            var Q11;
            Q11=makeQuery(id+"F0.imprint","IMPRINT",FACE,{"disambiguationData":[TD([[makeQuery(id+"F0.imprint","IMPRINT",EDGE,{"derivedFrom":sQuery(id+"F0.wireOp",EDGE,"E31.5")}),1.0]])]});
            extrude(context, id + "F6", {"entities" : qUnion([Q0, Q1, Q2, Q3, Q4, Q5, Q6, Q7, Q8, Q9, Q10, Q11]), "depth" : 79.8 * mm, "hasSecondDirection" : true, "secondDirectionOppositeDirection" : false, "secondDirectionDepth" : 73.8 * mm});
        }
        {
            var Q0;
            Q0=sQuery(id+"F0.wireOp",VERTEX,"E17");
            var Q1;
            Q1=sQuery(id+"F0.wireOp",VERTEX,"E22");
            var Q2;
            Q2=sQuery(id+"F0.wireOp",VERTEX,"E21");
            var Q3;
            Q3=sQuery(id+"F0.wireOp",VERTEX,"E20");
            var Q4;
            Q4=sQuery(id+"F0.wireOp",VERTEX,"E19");
            var Q5;
            Q5=sQuery(id+"F0.wireOp",VERTEX,"E18");
            var Q6;
            Q6=makeQuery(id+"F4.opExtrude","SWEPT_BODY",BODY,{"disambiguationData":[OSD([sQuery(id+"F0.wireOp",EDGE,"E23.0"),sQuery(id+"F0.wireOp",EDGE,"E23.1"),sQuery(id+"F0.wireOp",EDGE,"E23.2"),sQuery(id+"F0.wireOp",EDGE,"E23.3"),sQuery(id+"F0.wireOp",EDGE,"E23.4"),sQuery(id+"F0.wireOp",EDGE,"E23.5")])]});
            var Q7;
            Q7=makeQuery(id+"F4.opExtrude","SWEPT_BODY",BODY,{"disambiguationData":[OSD([sQuery(id+"F0.wireOp",EDGE,"E24.0"),sQuery(id+"F0.wireOp",EDGE,"E24.1"),sQuery(id+"F0.wireOp",EDGE,"E24.2"),sQuery(id+"F0.wireOp",EDGE,"E24.3"),sQuery(id+"F0.wireOp",EDGE,"E24.4"),sQuery(id+"F0.wireOp",EDGE,"E24.5")])]});
            var Q8;
            Q8=makeQuery(id+"F4.opExtrude","SWEPT_BODY",BODY,{"disambiguationData":[OSD([sQuery(id+"F0.wireOp",EDGE,"E25.0"),sQuery(id+"F0.wireOp",EDGE,"E25.1"),sQuery(id+"F0.wireOp",EDGE,"E25.2"),sQuery(id+"F0.wireOp",EDGE,"E25.3"),sQuery(id+"F0.wireOp",EDGE,"E25.4"),sQuery(id+"F0.wireOp",EDGE,"E25.5")])]});
            var Q9;
            Q9=makeQuery(id+"F4.opExtrude","SWEPT_BODY",BODY,{"disambiguationData":[OSD([sQuery(id+"F0.wireOp",EDGE,"E26.0"),sQuery(id+"F0.wireOp",EDGE,"E26.1"),sQuery(id+"F0.wireOp",EDGE,"E26.2"),sQuery(id+"F0.wireOp",EDGE,"E26.3"),sQuery(id+"F0.wireOp",EDGE,"E26.4"),sQuery(id+"F0.wireOp",EDGE,"E26.5")])]});
            var Q10;
            Q10=makeQuery(id+"F4.opExtrude","SWEPT_BODY",BODY,{"disambiguationData":[OSD([sQuery(id+"F0.wireOp",EDGE,"E27.0"),sQuery(id+"F0.wireOp",EDGE,"E27.1"),sQuery(id+"F0.wireOp",EDGE,"E27.2"),sQuery(id+"F0.wireOp",EDGE,"E27.3"),sQuery(id+"F0.wireOp",EDGE,"E27.4"),sQuery(id+"F0.wireOp",EDGE,"E27.5")])]});
            var Q11;
            Q11=makeQuery(id+"F4.opExtrude","SWEPT_BODY",BODY,{"disambiguationData":[OSD([sQuery(id+"F0.wireOp",EDGE,"E28.0"),sQuery(id+"F0.wireOp",EDGE,"E28.1"),sQuery(id+"F0.wireOp",EDGE,"E28.2"),sQuery(id+"F0.wireOp",EDGE,"E28.3"),sQuery(id+"F0.wireOp",EDGE,"E28.4"),sQuery(id+"F0.wireOp",EDGE,"E28.5")])]});
            hole(context, id + "F7", {"style" : HoleStyle.SIMPLE, "endStyle" : HoleEndStyle.THROUGH, "oppositeDirection" : true, "standardTappedOrClearance" : lookupTablePath({ "standard" : "ANSI", "fit" : "Close", "size" : "1/4", "type" : "Clearance" }), "standardBlindInLast" : lookupTablePath({ "fit" : "Close", "standard" : "ANSI", "size" : "1/4", "type" : "Clearance" }), "holeDiameter" : 6.53 * mm, "tappedDepth" : 12 * mm, "tapClearance" : 3, "locations" : qUnion([Q0, Q1, Q2, Q3, Q4, Q5]), "scope" : qUnion([Q6, Q7, Q8, Q9, Q10, Q11])});
        }
        {
            var Q0;
            Q0=makeQuery(id+"F1.opExtrude","SWEPT_BODY",BODY,{"disambiguationData":[OSD([sQuery(id+"F0.wireOp",EDGE,"E0.0"),sQuery(id+"F0.wireOp",EDGE,"E0.1"),sQuery(id+"F0.wireOp",EDGE,"E0.2"),sQuery(id+"F0.wireOp",EDGE,"E0.3"),sQuery(id+"F0.wireOp",EDGE,"E0.4"),sQuery(id+"F0.wireOp",EDGE,"E0.5"),sQuery(id+"F0.wireOp",EDGE,"E3.0"),sQuery(id+"F0.wireOp",EDGE,"E3.1"),sQuery(id+"F0.wireOp",EDGE,"E3.2"),sQuery(id+"F0.wireOp",EDGE,"E3.3"),sQuery(id+"F0.wireOp",EDGE,"E3.4"),sQuery(id+"F0.wireOp",EDGE,"E3.5"),sQuery(id+"F0.wireOp",EDGE,"E11.filletArc"),sQuery(id+"F0.wireOp",EDGE,"E12.filletArc"),sQuery(id+"F0.wireOp",EDGE,"E13.filletArc"),sQuery(id+"F0.wireOp",EDGE,"E14.filletArc"),sQuery(id+"F0.wireOp",EDGE,"E15.filletArc"),sQuery(id+"F0.wireOp",EDGE,"E16.filletArc")])]});
            var Q1;
            Q1=makeQuery(id+"F1.opExtrude","SWEPT_BODY",BODY,{"disambiguationData":[OSD([sQuery(id+"F0.wireOp",EDGE,"E4.0"),sQuery(id+"F0.wireOp",EDGE,"E4.1"),sQuery(id+"F0.wireOp",EDGE,"E4.2"),sQuery(id+"F0.wireOp",EDGE,"E4.3"),sQuery(id+"F0.wireOp",EDGE,"E4.4"),sQuery(id+"F0.wireOp",EDGE,"E4.5")])]});
            var Q2;
            Q2=makeQuery(id+"F2.opExtrude","SWEPT_BODY",BODY,{"disambiguationData":[OSD([sQuery(id+"F0.wireOp",EDGE,"E3.0"),sQuery(id+"F0.wireOp",EDGE,"E3.1"),sQuery(id+"F0.wireOp",EDGE,"E3.2"),sQuery(id+"F0.wireOp",EDGE,"E3.3"),sQuery(id+"F0.wireOp",EDGE,"E3.4"),sQuery(id+"F0.wireOp",EDGE,"E3.5"),sQuery(id+"F0.wireOp",EDGE,"E4.0"),sQuery(id+"F0.wireOp",EDGE,"E4.1"),sQuery(id+"F0.wireOp",EDGE,"E4.2"),sQuery(id+"F0.wireOp",EDGE,"E4.3"),sQuery(id+"F0.wireOp",EDGE,"E4.4"),sQuery(id+"F0.wireOp",EDGE,"E4.5"),sQuery(id+"F0.wireOp",EDGE,"E11.filletArc"),sQuery(id+"F0.wireOp",EDGE,"E12.filletArc"),sQuery(id+"F0.wireOp",EDGE,"E13.filletArc"),sQuery(id+"F0.wireOp",EDGE,"E14.filletArc"),sQuery(id+"F0.wireOp",EDGE,"E15.filletArc"),sQuery(id+"F0.wireOp",EDGE,"E16.filletArc")])]});
            var Q3;
            Q3=makeQuery(id+"F4.opExtrude","SWEPT_BODY",BODY,{"disambiguationData":[OSD([sQuery(id+"F0.wireOp",EDGE,"E23.0"),sQuery(id+"F0.wireOp",EDGE,"E23.1"),sQuery(id+"F0.wireOp",EDGE,"E23.2"),sQuery(id+"F0.wireOp",EDGE,"E23.3"),sQuery(id+"F0.wireOp",EDGE,"E23.4"),sQuery(id+"F0.wireOp",EDGE,"E23.5")])]});
            var Q4;
            Q4=makeQuery(id+"F4.opExtrude","SWEPT_BODY",BODY,{"disambiguationData":[OSD([sQuery(id+"F0.wireOp",EDGE,"E24.0"),sQuery(id+"F0.wireOp",EDGE,"E24.1"),sQuery(id+"F0.wireOp",EDGE,"E24.2"),sQuery(id+"F0.wireOp",EDGE,"E24.3"),sQuery(id+"F0.wireOp",EDGE,"E24.4"),sQuery(id+"F0.wireOp",EDGE,"E24.5")])]});
            var Q5;
            Q5=makeQuery(id+"F4.opExtrude","SWEPT_BODY",BODY,{"disambiguationData":[OSD([sQuery(id+"F0.wireOp",EDGE,"E25.0"),sQuery(id+"F0.wireOp",EDGE,"E25.1"),sQuery(id+"F0.wireOp",EDGE,"E25.2"),sQuery(id+"F0.wireOp",EDGE,"E25.3"),sQuery(id+"F0.wireOp",EDGE,"E25.4"),sQuery(id+"F0.wireOp",EDGE,"E25.5")])]});
            var Q6;
            Q6=makeQuery(id+"F4.opExtrude","SWEPT_BODY",BODY,{"disambiguationData":[OSD([sQuery(id+"F0.wireOp",EDGE,"E26.0"),sQuery(id+"F0.wireOp",EDGE,"E26.1"),sQuery(id+"F0.wireOp",EDGE,"E26.2"),sQuery(id+"F0.wireOp",EDGE,"E26.3"),sQuery(id+"F0.wireOp",EDGE,"E26.4"),sQuery(id+"F0.wireOp",EDGE,"E26.5")])]});
            var Q7;
            Q7=makeQuery(id+"F4.opExtrude","SWEPT_BODY",BODY,{"disambiguationData":[OSD([sQuery(id+"F0.wireOp",EDGE,"E27.0"),sQuery(id+"F0.wireOp",EDGE,"E27.1"),sQuery(id+"F0.wireOp",EDGE,"E27.2"),sQuery(id+"F0.wireOp",EDGE,"E27.3"),sQuery(id+"F0.wireOp",EDGE,"E27.4"),sQuery(id+"F0.wireOp",EDGE,"E27.5")])]});
            var Q8;
            Q8=makeQuery(id+"F4.opExtrude","SWEPT_BODY",BODY,{"disambiguationData":[OSD([sQuery(id+"F0.wireOp",EDGE,"E28.0"),sQuery(id+"F0.wireOp",EDGE,"E28.1"),sQuery(id+"F0.wireOp",EDGE,"E28.2"),sQuery(id+"F0.wireOp",EDGE,"E28.3"),sQuery(id+"F0.wireOp",EDGE,"E28.4"),sQuery(id+"F0.wireOp",EDGE,"E28.5")])]});
            var Q9;
            Q9=makeQuery(id+"F6.opExtrude","SWEPT_BODY",BODY,{"disambiguationData":[OSD([sQuery(id+"F0.wireOp",EDGE,"E1.0"),sQuery(id+"F0.wireOp",EDGE,"E23.0"),sQuery(id+"F0.wireOp",EDGE,"E23.1"),sQuery(id+"F0.wireOp",EDGE,"E23.2"),sQuery(id+"F0.wireOp",EDGE,"E23.3"),sQuery(id+"F0.wireOp",EDGE,"E23.4"),sQuery(id+"F0.wireOp",EDGE,"E23.5"),sQuery(id+"F0.wireOp",EDGE,"E34.0"),sQuery(id+"F0.wireOp",EDGE,"E34.1"),sQuery(id+"F0.wireOp",EDGE,"E34.2"),sQuery(id+"F0.wireOp",EDGE,"E34.4"),sQuery(id+"F0.wireOp",EDGE,"E34.5"),sQuery(id+"F0.wireOp",EDGE,"E35"),sQuery(id+"F0.wireOp",EDGE,"E36"),sQuery(id+"F0.wireOp",EDGE,"E37.filletArc"),sQuery(id+"F0.wireOp",EDGE,"E38.filletArc"),sQuery(id+"F0.wireOp",EDGE,"E39.filletArc"),sQuery(id+"F0.wireOp",EDGE,"E40.filletArc")])]});
            var Q10;
            Q10=makeQuery(id+"F6.opExtrude","SWEPT_BODY",BODY,{"disambiguationData":[OSD([sQuery(id+"F0.wireOp",EDGE,"E1.1"),sQuery(id+"F0.wireOp",EDGE,"E27.0"),sQuery(id+"F0.wireOp",EDGE,"E27.1"),sQuery(id+"F0.wireOp",EDGE,"E27.2"),sQuery(id+"F0.wireOp",EDGE,"E27.3"),sQuery(id+"F0.wireOp",EDGE,"E27.4"),sQuery(id+"F0.wireOp",EDGE,"E27.5"),sQuery(id+"F0.wireOp",EDGE,"E29.0"),sQuery(id+"F0.wireOp",EDGE,"E29.1"),sQuery(id+"F0.wireOp",EDGE,"E29.2"),sQuery(id+"F0.wireOp",EDGE,"E29.3"),sQuery(id+"F0.wireOp",EDGE,"E29.5"),sQuery(id+"F0.wireOp",EDGE,"E65.filletArc"),sQuery(id+"F0.wireOp",EDGE,"E66.filletArc"),sQuery(id+"F0.wireOp",EDGE,"E67.filletArc"),sQuery(id+"F0.wireOp",EDGE,"E68.filletArc"),sQuery(id+"F0.wireOp",EDGE,"E69"),sQuery(id+"F0.wireOp",EDGE,"E70")])]});
            var Q11;
            Q11=makeQuery(id+"F6.opExtrude","SWEPT_BODY",BODY,{"disambiguationData":[OSD([sQuery(id+"F0.wireOp",EDGE,"E1.2"),sQuery(id+"F0.wireOp",EDGE,"E28.0"),sQuery(id+"F0.wireOp",EDGE,"E28.1"),sQuery(id+"F0.wireOp",EDGE,"E28.2"),sQuery(id+"F0.wireOp",EDGE,"E28.3"),sQuery(id+"F0.wireOp",EDGE,"E28.4"),sQuery(id+"F0.wireOp",EDGE,"E28.5"),sQuery(id+"F0.wireOp",EDGE,"E30.0"),sQuery(id+"F0.wireOp",EDGE,"E30.1"),sQuery(id+"F0.wireOp",EDGE,"E30.2"),sQuery(id+"F0.wireOp",EDGE,"E30.3"),sQuery(id+"F0.wireOp",EDGE,"E30.5"),sQuery(id+"F0.wireOp",EDGE,"E59.filletArc"),sQuery(id+"F0.wireOp",EDGE,"E60.filletArc"),sQuery(id+"F0.wireOp",EDGE,"E61.filletArc"),sQuery(id+"F0.wireOp",EDGE,"E62.filletArc"),sQuery(id+"F0.wireOp",EDGE,"E63"),sQuery(id+"F0.wireOp",EDGE,"E64")])]});
            var Q12;
            Q12=makeQuery(id+"F6.opExtrude","SWEPT_BODY",BODY,{"disambiguationData":[OSD([sQuery(id+"F0.wireOp",EDGE,"E1.3"),sQuery(id+"F0.wireOp",EDGE,"E26.0"),sQuery(id+"F0.wireOp",EDGE,"E26.1"),sQuery(id+"F0.wireOp",EDGE,"E26.2"),sQuery(id+"F0.wireOp",EDGE,"E26.3"),sQuery(id+"F0.wireOp",EDGE,"E26.4"),sQuery(id+"F0.wireOp",EDGE,"E26.5"),sQuery(id+"F0.wireOp",EDGE,"E31.0"),sQuery(id+"F0.wireOp",EDGE,"E31.1"),sQuery(id+"F0.wireOp",EDGE,"E31.2"),sQuery(id+"F0.wireOp",EDGE,"E31.3"),sQuery(id+"F0.wireOp",EDGE,"E31.4"),sQuery(id+"F0.wireOp",EDGE,"E53.filletArc"),sQuery(id+"F0.wireOp",EDGE,"E54.filletArc"),sQuery(id+"F0.wireOp",EDGE,"E55.filletArc"),sQuery(id+"F0.wireOp",EDGE,"E56.filletArc"),sQuery(id+"F0.wireOp",EDGE,"E57"),sQuery(id+"F0.wireOp",EDGE,"E58")])]});
            var Q13;
            Q13=makeQuery(id+"F6.opExtrude","SWEPT_BODY",BODY,{"disambiguationData":[OSD([sQuery(id+"F0.wireOp",EDGE,"E1.4"),sQuery(id+"F0.wireOp",EDGE,"E25.0"),sQuery(id+"F0.wireOp",EDGE,"E25.1"),sQuery(id+"F0.wireOp",EDGE,"E25.2"),sQuery(id+"F0.wireOp",EDGE,"E25.3"),sQuery(id+"F0.wireOp",EDGE,"E25.4"),sQuery(id+"F0.wireOp",EDGE,"E25.5"),sQuery(id+"F0.wireOp",EDGE,"E32.0"),sQuery(id+"F0.wireOp",EDGE,"E32.1"),sQuery(id+"F0.wireOp",EDGE,"E32.2"),sQuery(id+"F0.wireOp",EDGE,"E32.3"),sQuery(id+"F0.wireOp",EDGE,"E32.5"),sQuery(id+"F0.wireOp",EDGE,"E47.filletArc"),sQuery(id+"F0.wireOp",EDGE,"E48.filletArc"),sQuery(id+"F0.wireOp",EDGE,"E49.filletArc"),sQuery(id+"F0.wireOp",EDGE,"E50.filletArc"),sQuery(id+"F0.wireOp",EDGE,"E51"),sQuery(id+"F0.wireOp",EDGE,"E52")])]});
            var Q14;
            Q14=makeQuery(id+"F6.opExtrude","SWEPT_BODY",BODY,{"disambiguationData":[OSD([sQuery(id+"F0.wireOp",EDGE,"E1.5"),sQuery(id+"F0.wireOp",EDGE,"E24.0"),sQuery(id+"F0.wireOp",EDGE,"E24.1"),sQuery(id+"F0.wireOp",EDGE,"E24.2"),sQuery(id+"F0.wireOp",EDGE,"E24.3"),sQuery(id+"F0.wireOp",EDGE,"E24.4"),sQuery(id+"F0.wireOp",EDGE,"E24.5"),sQuery(id+"F0.wireOp",EDGE,"E33.0"),sQuery(id+"F0.wireOp",EDGE,"E33.2"),sQuery(id+"F0.wireOp",EDGE,"E33.3"),sQuery(id+"F0.wireOp",EDGE,"E33.4"),sQuery(id+"F0.wireOp",EDGE,"E33.5"),sQuery(id+"F0.wireOp",EDGE,"E41.filletArc"),sQuery(id+"F0.wireOp",EDGE,"E42.filletArc"),sQuery(id+"F0.wireOp",EDGE,"E43.filletArc"),sQuery(id+"F0.wireOp",EDGE,"E44.filletArc"),sQuery(id+"F0.wireOp",EDGE,"E45"),sQuery(id+"F0.wireOp",EDGE,"E46")])]});
            booleanBodies(context, id + "F8", {"operationType" : BooleanOperationType.UNION, "tools" : qUnion([Q0, Q1, Q2, Q3, Q4, Q5, Q6, Q7, Q8, Q9, Q10, Q11, Q12, Q13, Q14])});
        }
        {
            var Q0;
            {var subQ0=sQuery(id+"F0.wireOp",EDGE,"E0.5");var subQ1=sQuery(id+"F0.wireOp",EDGE,"E0.4");var subQ2=sQuery(id+"F0.wireOp",EDGE,"E0.3");var subQ3=sQuery(id+"F0.wireOp",EDGE,"E0.2");var subQ4=sQuery(id+"F0.wireOp",EDGE,"E0.1");var subQ5=sQuery(id+"F0.wireOp",EDGE,"E0.0");var subQ6=sQuery(id+"F0.wireOp",EDGE,"E16.filletArc");var subQ7=sQuery(id+"F0.wireOp",EDGE,"E15.filletArc");var subQ8=sQuery(id+"F0.wireOp",EDGE,"E14.filletArc");var subQ9=sQuery(id+"F0.wireOp",EDGE,"E13.filletArc");var subQ10=sQuery(id+"F0.wireOp",EDGE,"E12.filletArc");var subQ11=sQuery(id+"F0.wireOp",EDGE,"E11.filletArc");var subQ12=sQuery(id+"F0.wireOp",EDGE,"E3.5");var subQ13=sQuery(id+"F0.wireOp",EDGE,"E3.4");var subQ14=sQuery(id+"F0.wireOp",EDGE,"E3.3");var subQ15=sQuery(id+"F0.wireOp",EDGE,"E3.2");var subQ16=sQuery(id+"F0.wireOp",EDGE,"E3.1");var subQ17=sQuery(id+"F0.wireOp",EDGE,"E3.0");var subQ18=sQuery(id+"F0.wireOp",EDGE,"E4.5");var subQ19=sQuery(id+"F0.wireOp",EDGE,"E4.4");var subQ20=sQuery(id+"F0.wireOp",EDGE,"E4.3");var subQ21=sQuery(id+"F0.wireOp",EDGE,"E4.2");var subQ22=sQuery(id+"F0.wireOp",EDGE,"E4.1");var subQ23=sQuery(id+"F0.wireOp",EDGE,"E4.0");Q0=makeQuery(id+"F8.opBoolean","MERGE",FACE,{"derivedFrom":[makeQuery(id+"F1.opExtrude","CAP_FACE",FACE,{"disambiguationData":[OSD([subQ23,subQ22,subQ21,subQ20,subQ19,subQ18])],"isStart":true}),makeQuery(id+"F2.opExtrude","CAP_FACE",FACE,{"disambiguationData":[OSD([subQ17,subQ16,subQ15,subQ14,subQ13,subQ12,subQ23,subQ22,subQ21,subQ20,subQ19,subQ18,subQ11,subQ10,subQ9,subQ8,subQ7,subQ6])],"isStart":true}),makeQuery(id+"F3.boolean.opBoolean","MERGE",FACE,{"derivedFrom":[makeQuery(id+"F1.opExtrude","CAP_FACE",FACE,{"disambiguationData":[OSD([subQ5,subQ4,subQ3,subQ2,subQ1,subQ0,subQ17,subQ16,subQ15,subQ14,subQ13,subQ12,subQ11,subQ10,subQ9,subQ8,subQ7,subQ6])],"isStart":true}),makeQuery(id+"F3.opExtrude","CAP_FACE",FACE,{"disambiguationData":[OSD([subQ5,subQ4,subQ3,subQ2,subQ1,subQ0,sQuery(id+"F0.wireOp",EDGE,"E1.0"),sQuery(id+"F0.wireOp",EDGE,"E1.1"),sQuery(id+"F0.wireOp",EDGE,"E1.2"),sQuery(id+"F0.wireOp",EDGE,"E1.3"),sQuery(id+"F0.wireOp",EDGE,"E1.4"),sQuery(id+"F0.wireOp",EDGE,"E1.5"),sQuery(id+"F0.wireOp",EDGE,"E5.filletArc"),sQuery(id+"F0.wireOp",EDGE,"E6.filletArc"),sQuery(id+"F0.wireOp",EDGE,"E7.filletArc"),sQuery(id+"F0.wireOp",EDGE,"E8.filletArc"),sQuery(id+"F0.wireOp",EDGE,"E9.filletArc"),sQuery(id+"F0.wireOp",EDGE,"E10.filletArc")])],"isStart":true})]})]});}
            fillet(context, id + "F9", {"entities" : qUnion([Q0]), "radius" : 1 * mm, "tangentPropagation" : true, "allowEdgeOverflow" : false});
        }
    });
